# Revit family: BE_99061_de_DE
name_source: partatom
category: Leuchten
revit_build: Autodesk Revit 2015 (Build: 20160512_0715(x64)
units: mm (PartAtom-declared; Revit-internal decimal feet)

## types (4) — shared parameters
AC/DC = AC
Aktualisierung = 2016-10-20T04:14:09
BEGA_Dummy = Nein
BEGA_IES = Ja
BEGA_Intern = Ja
BEGA_Intern_Konstruktion = Ja
BEGA_Intern_an = Ja
BEGA_Intern_aus = Ja
Beschreibung = Wegeleuchte
Beschreibung_Sonderanfertigung = Hier können Sie Informationen zur Sonderanfertigung eintragen.
CE_Konformität = ja
Energieeffizienzklasse = LED A++ - A
Farbfilter = 16777215
Farbtemperaturverschiebung bei Dämpfen der Lampe = <Keine Auswahl>
Farbwiedergabeindex = Ra > 80
Frequenz = 50-60 Hz
Gewicht = 48.0 kg
Hersteller = BEGA
Lampe = LED 50.4 W
Lastklassifizierung = Beleuchtung
Lebensdauerkriterien = L70 = 50.000 h
Logo = BEGA_Logo.png
M_W = Nein
Material_02 = BEGA_Oberfläche_Silber_matt
Material_03 = BEGA_Oberfläche_Weiss_matt
Material_06 = BEGA_Oberfläche_Edelstahl_gebürstet
Material_08 = BEGA_Oberfläche_Stahl_verzinkt
Material_09 = BEGA_Glas_klar
Material_10 = BEGA_Glas_matt
Material_11 = BEGA_Glas_opal
Material_15 = BEGA_Leuchtmedium_matt
Material_17 = BEGA_Reflektor
Material_18 = BEGA_Gummi_schwarz
Neigungswinkel = 0.00°
Produktdatenblatt = http://www.bega.de
Scheinlast = 0 VA
Schutzart = IP 65
Schutzklasse = I
Sonderanfertigung = Nein
Spannung = 240 V
Typenbild = 99061.png
URL = http://www.bega.de
Umgebungstemperatur = 25 °C
zero-valued in all types: Vorgabe-Ansicht

## per-type parameters (varying)
| type | Bestellnummer | Datei für fotometrisches Netz | Farbtemperatur | LED_Modulbezeichnung | Lampenlichtstrom | Leuchtenlichtstrom | M_A | M_G | Modell |
| BEGA_99061_Silber_K4 | 99061AK4 | BE_99061K4.IES | 4000 K | 4x LED-0462/840 | 7960 lm | 3559 lm | Ja | Nein | 99061AK4 |
| BEGA_99061_Grafit_K3 | 99061 | BE_99061.IES | 3000 K | 4x LED-0462/830 | 7280 lm | 3255 lm | Nein | Ja | 99061 |
| BEGA_99061_Grafit_K4 | 99061K4 | BE_99061K4.IES | 4000 K | 4x LED-0462/840 | 7960 lm | 3559 lm | Nein | Ja | 99061K4 |
| BEGA_99061_Silber_K3 | 99061A | BE_99061.IES | 3000 K | 4x LED-0462/830 | 7280 lm | 3255 lm | Ja | Nein | 99061A |
